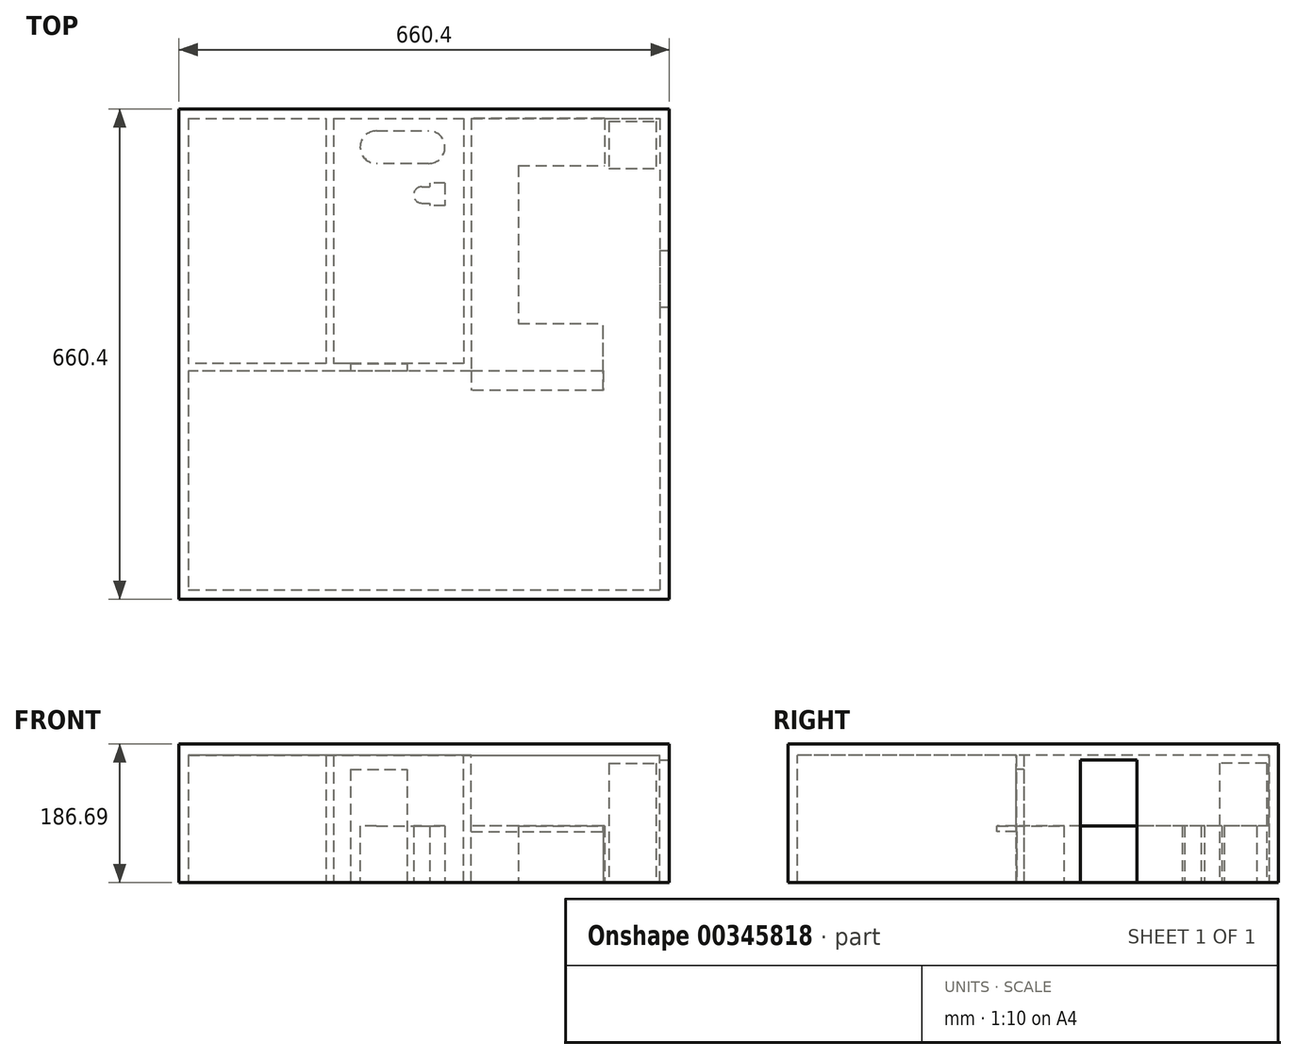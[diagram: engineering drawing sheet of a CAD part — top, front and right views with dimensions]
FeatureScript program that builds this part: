
annotation { "Feature Type Name" : "Feature", "Feature Type Description" : "" }
export const myFeature = defineFeature(function(context is Context, id is Id, definition is map)
    precondition{}
    {
        {
            var Q0;
            Q0=qCreatedBy(makeId("Top.planeOp"),FACE);
            var sketch = newSketch(context, id + "F0", { "sketchPlane" : qUnion([Q0])});
            skLineSegment(sketch, "E0.bottom", {"start": v(330.2, 330.2) * mm, "end": v(-330.2, 330.2) * mm});
            skLineSegment(sketch, "E0.top", {"start": v(330.2, -330.2) * mm, "end": v(-330.2, -330.2) * mm});
            skLineSegment(sketch, "E0.left", {"start": v(330.2, 330.2) * mm, "end": v(330.2, -330.2) * mm});
            skLineSegment(sketch, "E0.right", {"start": v(-330.2, 330.2) * mm, "end": v(-330.2, -330.2) * mm});
            skPoint(sketch, "E0.middle", {"position": v(0, 0) * mm});
            skSolve(sketch);
        }
        {
            var Q0;
            Q0=makeQuery(id+"F0.imprint","IMPRINT",FACE,{"disambiguationData":[TD([[makeQuery(id+"F0.imprint","IMPRINT",EDGE,{"derivedFrom":sQuery(id+"F0.wireOp",EDGE,"E0.bottom")}),1.0]])]});
            extrude(context, id + "F1", {"entities" : qUnion([Q0]), "depth" : 171.45 * mm});
        }
        {
            var Q0;
            Q0=qCreatedBy(makeId("Top.planeOp"),FACE);
            var sketch = newSketch(context, id + "F2", { "sketchPlane" : qUnion([Q0])});
            skLineSegment(sketch, "E1.bottom", {"start": v(327.63, 317.5) * mm, "end": v(-327.63, 317.5) * mm});
            skLineSegment(sketch, "E1.top", {"start": v(327.63, -317.5) * mm, "end": v(-327.63, -317.5) * mm});
            skLineSegment(sketch, "E1.left", {"start": v(327.63, 317.5) * mm, "end": v(327.63, -317.5) * mm});
            skLineSegment(sketch, "E1.right", {"start": v(-327.63, 317.5) * mm, "end": v(-327.63, -317.5) * mm});
            skPoint(sketch, "E1.middle", {"position": v(0, 0) * mm});
            skSolve(sketch);
        }
        {
            var Q0;
            Q0=makeQuery(id+"F1.opExtrude","CAP_FACE",FACE,{"disambiguationData":[OSD([sQuery(id+"F0.wireOp",EDGE,"E0.bottom"),sQuery(id+"F0.wireOp",EDGE,"E0.top"),sQuery(id+"F0.wireOp",EDGE,"E0.left"),sQuery(id+"F0.wireOp",EDGE,"E0.right")])],"isStart":false});
            var sketch = newSketch(context, id + "F3", { "sketchPlane" : qUnion([Q0])});
            skLineSegment(sketch, "E2.bottom", {"start": v(-317.5, 317.5) * mm, "end": v(317.5, 317.5) * mm});
            skLineSegment(sketch, "E2.top", {"start": v(-317.5, -317.5) * mm, "end": v(317.5, -317.5) * mm});
            skLineSegment(sketch, "E2.left", {"start": v(-317.5, 317.5) * mm, "end": v(-317.5, -317.5) * mm});
            skLineSegment(sketch, "E2.right", {"start": v(317.5, 317.5) * mm, "end": v(317.5, -317.5) * mm});
            skPoint(sketch, "E2.middle", {"position": v(0, 0) * mm});
            skSolve(sketch);
        }
        {
            var Q0;
            Q0=makeQuery(id+"F3.imprint","IMPRINT",FACE,{"disambiguationData":[TD([[makeQuery(id+"F3.imprint","IMPRINT",EDGE,{"derivedFrom":sQuery(id+"F3.wireOp",EDGE,"E2.bottom")}),-1.0]])]});
            extrude(context, id + "F4", {"entities" : qUnion([Q0]), "operationType" : NewBodyOperationType.REMOVE, "oppositeDirection" : true, "depth" : 251.46 * mm});
        }
        {
            var Q0;
            Q0=makeQuery(id+"F1.opExtrude","SWEPT_FACE",FACE,{"disambiguationData":[OSD([sQuery(id+"F0.wireOp",EDGE,"E0.left")])]});
            var sketch = newSketch(context, id + "F5", { "sketchPlane" : qUnion([Q0])});
            skLineSegment(sketch, "E3.bottom", {"start": v(139.7, 0) * mm, "end": v(63.5, 0) * mm});
            skLineSegment(sketch, "E3.top", {"start": v(139.7, 165.1) * mm, "end": v(63.5, 165.1) * mm});
            skLineSegment(sketch, "E3.left", {"start": v(139.7, 0) * mm, "end": v(139.7, 165.1) * mm});
            skLineSegment(sketch, "E3.right", {"start": v(63.5, 0) * mm, "end": v(63.5, 165.1) * mm});
            skSolve(sketch);
        }
        {
            var Q0;
            Q0=makeQuery(id+"F5.imprint","IMPRINT",FACE,{"disambiguationData":[TD([[makeQuery(id+"F5.imprint","IMPRINT",EDGE,{"derivedFrom":sQuery(id+"F5.wireOp",EDGE,"E3.bottom")}),-1.0]])]});
            var Q1;
            Q1=makeQuery(id+"F4.boolean.opBoolean","COPY",FACE,{"derivedFrom":makeQuery(id+"F4.opExtrude","SWEPT_FACE",FACE,{"disambiguationData":[OSD([sQuery(id+"F3.wireOp",EDGE,"E2.right")])]})});
            extrude(context, id + "F6", {"entities" : qUnion([Q0]), "operationType" : NewBodyOperationType.REMOVE, "endBound" : BoundingType.UP_TO_SURFACE, "oppositeDirection" : true, "endBoundEntityFace" : qUnion([Q1]), "depth" : 25.4 * mm});
        }
        {
            var Q0;
            Q0=makeQuery(id+"F2.imprint","IMPRINT",FACE,{"disambiguationData":[TD([[makeQuery(id+"F2.imprint","IMPRINT",EDGE,{"derivedFrom":sQuery(id+"F2.wireOp",EDGE,"E1.bottom")}),1.0]])]});
            var sketch = newSketch(context, id + "F7", { "sketchPlane" : qUnion([Q0])});
            skLineSegment(sketch, "E4.bottom", {"start": v(317.5, -22.86) * mm, "end": v(-317.5, -22.86) * mm});
            skLineSegment(sketch, "E4.top", {"start": v(317.5, -12.7) * mm, "end": v(-317.5, -12.7) * mm});
            skLineSegment(sketch, "E4.left", {"start": v(317.5, -22.86) * mm, "end": v(317.5, -12.7) * mm});
            skLineSegment(sketch, "E4.right", {"start": v(-317.5, -22.86) * mm, "end": v(-317.5, -12.7) * mm});
            skSolve(sketch);
        }
        {
            var Q0;
            Q0=makeQuery(id+"F7.imprint","IMPRINT",FACE,{"disambiguationData":[TD([[makeQuery(id+"F7.imprint","IMPRINT",EDGE,{"derivedFrom":sQuery(id+"F7.wireOp",EDGE,"E4.bottom")}),-1.0]])]});
            var Q1;
            Q1=makeQuery(id+"F1.opExtrude","CAP_FACE",FACE,{"disambiguationData":[OSD([sQuery(id+"F0.wireOp",EDGE,"E0.bottom"),sQuery(id+"F0.wireOp",EDGE,"E0.top"),sQuery(id+"F0.wireOp",EDGE,"E0.left"),sQuery(id+"F0.wireOp",EDGE,"E0.right")])],"isStart":false});
            extrude(context, id + "F8", {"entities" : qUnion([Q0]), "operationType" : NewBodyOperationType.ADD, "endBound" : BoundingType.UP_TO_SURFACE, "endBoundEntityFace" : qUnion([Q1]), "depth" : 104.14 * mm});
        }
        {
            var Q0;
            Q0=makeQuery(id+"F8.opExtrude","SWEPT_FACE",FACE,{"disambiguationData":[OSD([sQuery(id+"F7.wireOp",EDGE,"E4.bottom")])]});
            var sketch = newSketch(context, id + "F9", { "sketchPlane" : qUnion([Q0])});
            skLineSegment(sketch, "E5.bottom", {"start": v(317.5, 0) * mm, "end": v(63.5, 0) * mm});
            skLineSegment(sketch, "E5.top", {"start": v(317.5, 171.45) * mm, "end": v(63.5, 171.45) * mm});
            skLineSegment(sketch, "E5.left", {"start": v(317.5, 0) * mm, "end": v(317.5, 171.45) * mm});
            skLineSegment(sketch, "E5.right", {"start": v(63.5, 0) * mm, "end": v(63.5, 171.45) * mm});
            skSolve(sketch);
        }
        {
            var Q0;
            Q0=makeQuery(id+"F9.imprint","IMPRINT",FACE,{"disambiguationData":[TD([[makeQuery(id+"F9.imprint","IMPRINT",EDGE,{"derivedFrom":sQuery(id+"F9.wireOp",EDGE,"E5.bottom")}),-1.0]])]});
            extrude(context, id + "F10", {"entities" : qUnion([Q0]), "operationType" : NewBodyOperationType.REMOVE, "endBound" : BoundingType.UP_TO_NEXT, "oppositeDirection" : true, "depth" : 25.4 * mm});
        }
        {
            var Q0;
            {var subQ0=sQuery(id+"F0.wireOp",EDGE,"E0.right");var subQ1=sQuery(id+"F0.wireOp",EDGE,"E0.left");var subQ2=sQuery(id+"F0.wireOp",EDGE,"E0.top");var subQ3=sQuery(id+"F0.wireOp",EDGE,"E0.bottom");Q0=makeQuery(id+"F8.boolean.opBoolean","MERGE",FACE,{"derivedFrom":[makeQuery(id+"F1.opExtrude","CAP_FACE",FACE,{"disambiguationData":[OSD([subQ3,subQ2,subQ1,subQ0])],"isStart":false}),makeQuery(id+"F8.opExtrude","CAP_FACE",FACE,{"disambiguationData":[OSD([subQ3,subQ2,subQ1,subQ0])],"isStart":false})]});}
            var sketch = newSketch(context, id + "F11", { "sketchPlane" : qUnion([Q0])});
            skLineSegment(sketch, "E6.bottom", {"start": v(-330.2, 330.2) * mm, "end": v(330.2, 330.2) * mm});
            skLineSegment(sketch, "E6.top", {"start": v(-330.2, -330.2) * mm, "end": v(330.2, -330.2) * mm});
            skLineSegment(sketch, "E6.left", {"start": v(-330.2, 330.2) * mm, "end": v(-330.2, -330.2) * mm});
            skLineSegment(sketch, "E6.right", {"start": v(330.2, 330.2) * mm, "end": v(330.2, -330.2) * mm});
            skSolve(sketch);
        }
        {
            var Q0;
            Q0 = qSketchRegion(id + "F11", true);
            extrude(context, id + "F12", {"entities" : qUnion([Q0]), "depth" : 15.24 * mm});
        }
        {
            var Q0;
            Q0=makeQuery(id+"F2.imprint","IMPRINT",FACE,{"disambiguationData":[TD([[makeQuery(id+"F2.imprint","IMPRINT",EDGE,{"derivedFrom":sQuery(id+"F2.wireOp",EDGE,"E1.bottom")}),1.0]])]});
            var sketch = newSketch(context, id + "F13", { "sketchPlane" : qUnion([Q0])});
            skArc(sketch, "E7", {"start": v(-64.4, 300.77) * mm, "mid": v(-86.36, 278.8) * mm, "end": v(-64.4, 256.84) * mm});
            skArc(sketch, "E8", {"start": v(5.98, 256.84) * mm, "mid": v(27.94, 278.8) * mm, "end": v(5.98, 300.77) * mm});
            skLineSegment(sketch, "E9", {"start": v(-64.4, 300.77) * mm, "end": v(5.98, 300.77) * mm});
            skLineSegment(sketch, "E10", {"start": v(5.98, 256.84) * mm, "end": v(-64.4, 256.84) * mm});
            skLineSegment(sketch, "E11.bottom", {"start": v(27.94, 230.47) * mm, "end": v(7.62, 230.47) * mm});
            skLineSegment(sketch, "E11.top", {"start": v(27.94, 200.06) * mm, "end": v(7.62, 200.06) * mm});
            skLineSegment(sketch, "E11.left", {"start": v(27.94, 230.47) * mm, "end": v(27.94, 200.06) * mm});
            skLineSegment(sketch, "E11.right", {"start": v(7.62, 230.47) * mm, "end": v(7.62, 200.06) * mm});
            skArc(sketch, "E12", {"start": v(-3.37, 225.46) * mm, "mid": v(-14.36, 214.47) * mm, "end": v(-3.37, 203.47) * mm});
            skLineSegment(sketch, "E13", {"start": v(-3.37, 225.46) * mm, "end": v(7.62, 225.46) * mm});
            skLineSegment(sketch, "E14", {"start": v(-3.37, 203.47) * mm, "end": v(7.62, 203.47) * mm});
            skSolve(sketch);
        }
        {
            var Q0;
            Q0=makeQuery(id+"F13.imprint","IMPRINT",FACE,{"disambiguationData":[TD([[makeQuery(id+"F13.imprint","IMPRINT",EDGE,{"derivedFrom":sQuery(id+"F13.wireOp",EDGE,"E7")}),1.0]])]});
            var Q1;
            {var subQ1=sQuery(id+"F13.wireOp",EDGE,"E11.bottom");Q1=makeQuery(id+"F13.imprint","IMPRINT",FACE,{"disambiguationData":[TD([[makeQuery(id+"F13.imprint","IMPRINT",EDGE,{"derivedFrom":subQ1}),1.0]])]});}
            var Q2;
            Q2=makeQuery(id+"F13.imprint","IMPRINT",FACE,{"disambiguationData":[TD([[makeQuery(id+"F13.imprint","IMPRINT",EDGE,{"derivedFrom":sQuery(id+"F13.wireOp",EDGE,"E12")}),1.0]])]});
            extrude(context, id + "F14", {"entities" : qUnion([Q0, Q1, Q2]), "depth" : 76.2 * mm});
        }
        {
            var Q0;
            Q0=makeQuery(id+"F8.opExtrude","SWEPT_FACE",FACE,{"disambiguationData":[OSD([sQuery(id+"F7.wireOp",EDGE,"E4.bottom")])]});
            var sketch = newSketch(context, id + "F15", { "sketchPlane" : qUnion([Q0])});
            skLineSegment(sketch, "E15.bottom", {"start": v(-23.3, 0) * mm, "end": v(-99.5, 0) * mm});
            skLineSegment(sketch, "E15.top", {"start": v(-23.3, 152.4) * mm, "end": v(-99.5, 152.4) * mm});
            skLineSegment(sketch, "E15.left", {"start": v(-23.3, 0) * mm, "end": v(-23.3, 152.4) * mm});
            skLineSegment(sketch, "E15.right", {"start": v(-99.5, 0) * mm, "end": v(-99.5, 152.4) * mm});
            skSolve(sketch);
        }
        {
            var Q0;
            Q0=makeQuery(id+"F15.imprint","IMPRINT",FACE,{"disambiguationData":[TD([[makeQuery(id+"F15.imprint","IMPRINT",EDGE,{"derivedFrom":sQuery(id+"F15.wireOp",EDGE,"E15.bottom")}),-1.0]])]});
            extrude(context, id + "F16", {"entities" : qUnion([Q0]), "operationType" : NewBodyOperationType.REMOVE, "endBound" : BoundingType.UP_TO_NEXT, "oppositeDirection" : true, "depth" : 25.4 * mm});
        }
        {
            var Q0;
            Q0=makeQuery(id+"F8.opExtrude","SWEPT_FACE",FACE,{"disambiguationData":[OSD([sQuery(id+"F7.wireOp",EDGE,"E4.top")])]});
            var sketch = newSketch(context, id + "F17", { "sketchPlane" : qUnion([Q0])});
            skLineSegment(sketch, "E16.bottom", {"start": v(-63.5, 0) * mm, "end": v(-53.34, 0) * mm});
            skLineSegment(sketch, "E16.top", {"start": v(-63.5, 171.45) * mm, "end": v(-53.34, 171.45) * mm});
            skLineSegment(sketch, "E16.left", {"start": v(-63.5, 0) * mm, "end": v(-63.5, 171.45) * mm});
            skLineSegment(sketch, "E16.right", {"start": v(-53.34, 0) * mm, "end": v(-53.34, 171.45) * mm});
            skSolve(sketch);
        }
        {
            var Q0;
            Q0=makeQuery(id+"F17.imprint","IMPRINT",FACE,{"disambiguationData":[TD([[makeQuery(id+"F17.imprint","IMPRINT",EDGE,{"derivedFrom":sQuery(id+"F17.wireOp",EDGE,"E16.bottom")}),1.0]])]});
            var Q1;
            Q1=makeQuery(id+"F4.boolean.opBoolean","COPY",FACE,{"derivedFrom":makeQuery(id+"F4.opExtrude","SWEPT_FACE",FACE,{"disambiguationData":[OSD([sQuery(id+"F3.wireOp",EDGE,"E2.bottom")])]})});
            extrude(context, id + "F18", {"entities" : qUnion([Q0]), "operationType" : NewBodyOperationType.ADD, "endBound" : BoundingType.UP_TO_SURFACE, "endBoundEntityFace" : qUnion([Q1]), "depth" : 25.4 * mm});
        }
        {
            var Q0;
            Q0=makeQuery(id+"F2.imprint","IMPRINT",FACE,{"disambiguationData":[TD([[makeQuery(id+"F2.imprint","IMPRINT",EDGE,{"derivedFrom":sQuery(id+"F2.wireOp",EDGE,"E1.bottom")}),1.0]])]});
            var sketch = newSketch(context, id + "F19", { "sketchPlane" : qUnion([Q0])});
            skLineSegment(sketch, "E17.bottom", {"start": v(63.5, 317.5) * mm, "end": v(127, 317.5) * mm});
            skLineSegment(sketch, "E17.top", {"start": v(63.5, -22.46) * mm, "end": v(127, -22.46) * mm});
            skLineSegment(sketch, "E17.left", {"start": v(63.5, 317.5) * mm, "end": v(63.5, -22.46) * mm});
            skLineSegment(sketch, "E17.right", {"start": v(127, 254) * mm, "end": v(127, 41.04) * mm});
            skLineSegment(sketch, "E18.bottom", {"start": v(63.5, -22.46) * mm, "end": v(240.89, -22.46) * mm});
            skLineSegment(sketch, "E18.top", {"start": v(127, 41.04) * mm, "end": v(240.89, 41.04) * mm});
            skLineSegment(sketch, "E18.left", {"start": v(63.5, -22.46) * mm, "end": v(63.5, 41.04) * mm});
            skLineSegment(sketch, "E18.right", {"start": v(240.89, -22.46) * mm, "end": v(240.89, 41.04) * mm});
            skLineSegment(sketch, "E19.bottom", {"start": v(63.5, 317.5) * mm, "end": v(242.7, 317.5) * mm});
            skLineSegment(sketch, "E19.top", {"start": v(127, 254) * mm, "end": v(242.7, 254) * mm});
            skLineSegment(sketch, "E19.left", {"start": v(63.5, 317.5) * mm, "end": v(63.5, 254) * mm});
            skLineSegment(sketch, "E19.right", {"start": v(242.7, 317.5) * mm, "end": v(242.7, 254) * mm});
            skSolve(sketch);
        }
        {
            var Q0;
            Q0=makeQuery(id+"F19.imprint","IMPRINT",FACE,{"disambiguationData":[TD([[makeQuery(id+"F19.imprint","IMPRINT",EDGE,{"derivedFrom":sQuery(id+"F19.wireOp",EDGE,"E17.left")}),1.0]])]});
            extrude(context, id + "F20", {"entities" : qUnion([Q0]), "depth" : 76.2 * mm});
        }
        {
            var Q0;
            Q0=makeQuery(id+"F2.imprint","IMPRINT",FACE,{"disambiguationData":[TD([[makeQuery(id+"F2.imprint","IMPRINT",EDGE,{"derivedFrom":sQuery(id+"F2.wireOp",EDGE,"E1.bottom")}),1.0]])]});
            var sketch = newSketch(context, id + "F21", { "sketchPlane" : qUnion([Q0])});
            skLineSegment(sketch, "E20.bottom", {"start": v(248.56, 313.85) * mm, "end": v(312.06, 313.85) * mm});
            skLineSegment(sketch, "E20.top", {"start": v(248.56, 250.35) * mm, "end": v(312.06, 250.35) * mm});
            skLineSegment(sketch, "E20.left", {"start": v(248.56, 313.85) * mm, "end": v(248.56, 250.35) * mm});
            skLineSegment(sketch, "E20.right", {"start": v(312.06, 313.85) * mm, "end": v(312.06, 250.35) * mm});
            skSolve(sketch);
        }
        {
            var Q0;
            Q0=makeQuery(id+"F21.imprint","IMPRINT",FACE,{"disambiguationData":[TD([[makeQuery(id+"F21.imprint","IMPRINT",EDGE,{"derivedFrom":sQuery(id+"F21.wireOp",EDGE,"E20.bottom")}),-1.0]])]});
            extrude(context, id + "F22", {"entities" : qUnion([Q0]), "depth" : 160.53 * mm});
        }
        {
            var Q0;
            Q0=makeQuery(id+"F2.imprint","IMPRINT",FACE,{"disambiguationData":[TD([[makeQuery(id+"F2.imprint","IMPRINT",EDGE,{"derivedFrom":sQuery(id+"F2.wireOp",EDGE,"E1.bottom")}),1.0]])]});
            var sketch = newSketch(context, id + "F23", { "sketchPlane" : qUnion([Q0])});
            skLineSegment(sketch, "E21.bottom", {"start": v(-132.2, 317.5) * mm, "end": v(-122.04, 317.5) * mm});
            skLineSegment(sketch, "E21.top", {"start": v(-132.2, -12.7) * mm, "end": v(-122.04, -12.7) * mm});
            skLineSegment(sketch, "E21.left", {"start": v(-132.2, 317.5) * mm, "end": v(-132.2, -12.7) * mm});
            skLineSegment(sketch, "E21.right", {"start": v(-122.04, 317.5) * mm, "end": v(-122.04, -12.7) * mm});
            skSolve(sketch);
        }
        {
            var Q0;
            Q0=makeQuery(id+"F23.imprint","IMPRINT",FACE,{"disambiguationData":[TD([[makeQuery(id+"F23.imprint","IMPRINT",EDGE,{"derivedFrom":sQuery(id+"F23.wireOp",EDGE,"E21.bottom")}),1.0]])]});
            extrude(context, id + "F24", {"entities" : qUnion([Q0]), "operationType" : NewBodyOperationType.ADD, "endBound" : BoundingType.UP_TO_NEXT, "depth" : 25.4 * mm});
        }
        {
            var Q0;
            Q0=makeQuery(id+"F20.opExtrude","CAP_FACE",FACE,{"disambiguationData":[OSD([sQuery(id+"F19.wireOp",EDGE,"E17.left"),sQuery(id+"F19.wireOp",EDGE,"E17.right"),sQuery(id+"F19.wireOp",EDGE,"E18.bottom"),sQuery(id+"F19.wireOp",EDGE,"E18.top"),sQuery(id+"F19.wireOp",EDGE,"E18.left"),sQuery(id+"F19.wireOp",EDGE,"E18.right"),sQuery(id+"F19.wireOp",EDGE,"E19.bottom"),sQuery(id+"F19.wireOp",EDGE,"E19.top"),sQuery(id+"F19.wireOp",EDGE,"E19.left"),sQuery(id+"F19.wireOp",EDGE,"E19.right")])],"isStart":false});
            var sketch = newSketch(context, id + "F25", { "sketchPlane" : qUnion([Q0])});
            skLineSegment(sketch, "E22.bottom", {"start": v(240.89, 5.44) * mm, "end": v(63.5, 5.44) * mm});
            skLineSegment(sketch, "E22.top", {"start": v(240.89, -48.97) * mm, "end": v(63.5, -48.97) * mm});
            skLineSegment(sketch, "E22.left", {"start": v(240.89, 5.44) * mm, "end": v(240.89, -48.97) * mm});
            skLineSegment(sketch, "E22.right", {"start": v(63.5, 5.44) * mm, "end": v(63.5, -48.97) * mm});
            skSolve(sketch);
        }
        {
            var Q0;
            Q0 = qSketchRegion(id + "F25", true);
            extrude(context, id + "F26", {"entities" : qUnion([Q0]), "operationType" : NewBodyOperationType.ADD, "oppositeDirection" : true, "depth" : 7.62 * mm});
        }
    });
